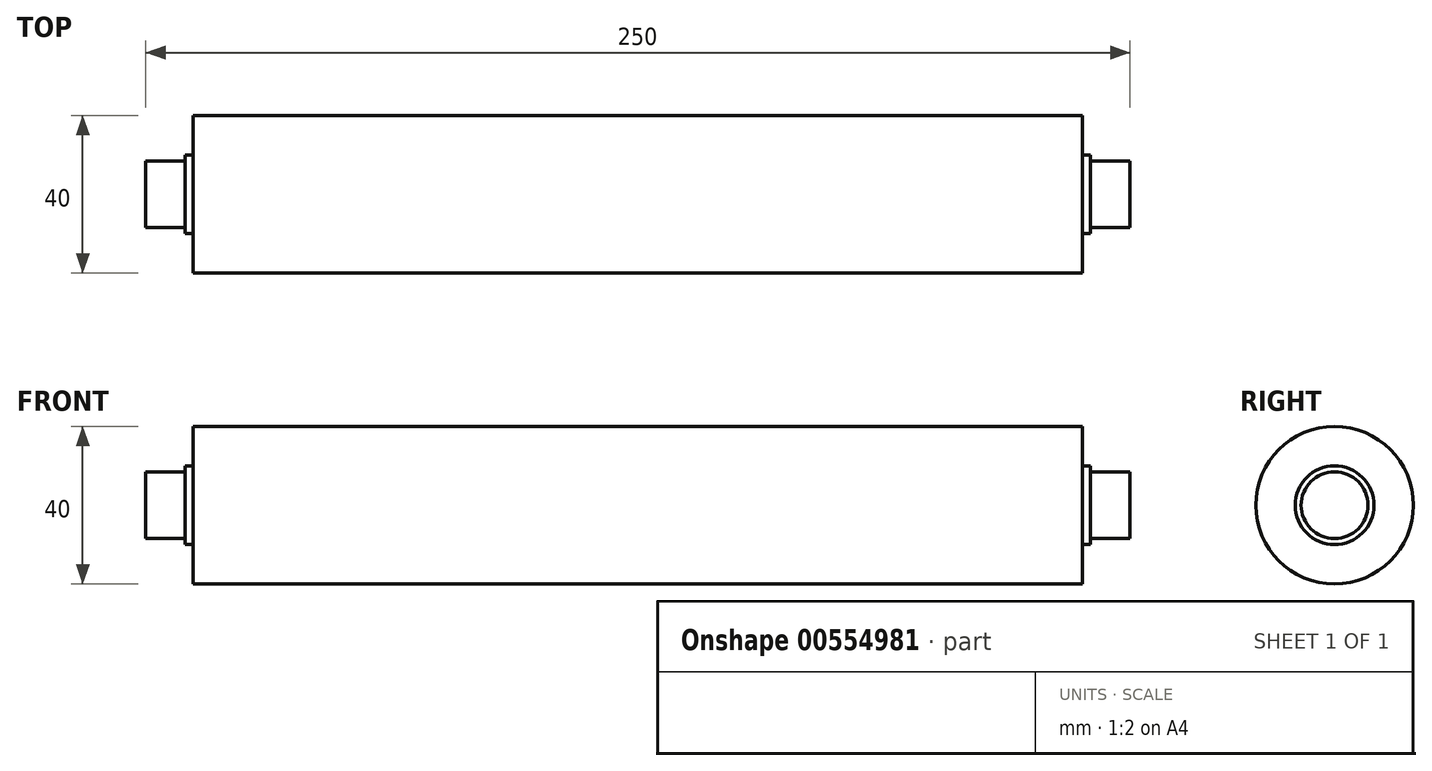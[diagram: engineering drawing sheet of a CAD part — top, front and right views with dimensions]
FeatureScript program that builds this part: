
annotation { "Feature Type Name" : "Feature", "Feature Type Description" : "" }
export const myFeature = defineFeature(function(context is Context, id is Id, definition is map)
    precondition{}
    {
        {
            var Q0;
            Q0=qCreatedBy(makeId("Front.planeOp"),FACE);
            var sketch = newSketch(context, id + "F0", { "sketchPlane" : qUnion([Q0])});
            skLineSegment(sketch, "E0", {"start": v(-125, 0) * mm, "end": v(-125, 8.5) * mm});
            skLineSegment(sketch, "E1", {"start": v(-125, 8.5) * mm, "end": v(-115, 8.5) * mm});
            skLineSegment(sketch, "E2", {"start": v(-115, 8.5) * mm, "end": v(-115, 10) * mm});
            skLineSegment(sketch, "E3", {"start": v(-115, 10) * mm, "end": v(-113, 10) * mm});
            skLineSegment(sketch, "E4", {"start": v(-113, 10) * mm, "end": v(-113, 20) * mm});
            skLineSegment(sketch, "E5", {"start": v(-113, 20) * mm, "end": v(113, 20) * mm});
            skLineSegment(sketch, "E6", {"start": v(113, 20) * mm, "end": v(113, 10) * mm});
            skLineSegment(sketch, "E7", {"start": v(113, 10) * mm, "end": v(115, 10) * mm});
            skLineSegment(sketch, "E8", {"start": v(115, 10) * mm, "end": v(115, 8.5) * mm});
            skPoint(sketch, "E8.endSnap0", {"position": v(-120, 8.5) * mm});
            skLineSegment(sketch, "E9", {"start": v(115, 8.5) * mm, "end": v(125, 8.5) * mm});
            skLineSegment(sketch, "E10", {"start": v(125, 8.5) * mm, "end": v(125, 0) * mm});
            skLineSegment(sketch, "E11", {"start": v(125, 0) * mm, "end": v(-125, 0) * mm});
            skLineSegment(sketch, "E12", {"start": v(0, 0) * mm, "end": v(0, 20) * mm, "construction": true});
            skSolve(sketch);
        }
        {
            var Q0;
            Q0=makeQuery(id+"F0.imprint","IMPRINT",FACE,{"disambiguationData":[TD([[makeQuery(id+"F0.imprint","IMPRINT",EDGE,{"derivedFrom":sQuery(id+"F0.wireOp",EDGE,"E0")}),-1.0]])]});
            var Q1;
            Q1=sQuery(id+"F0.wireOp",EDGE,"E11");
            revolve(context, id + "F1", {"entities" : qUnion([Q0]), "axis" : qUnion([Q1]), "revolveType" : RevolveType.FULL});
        }
    });
